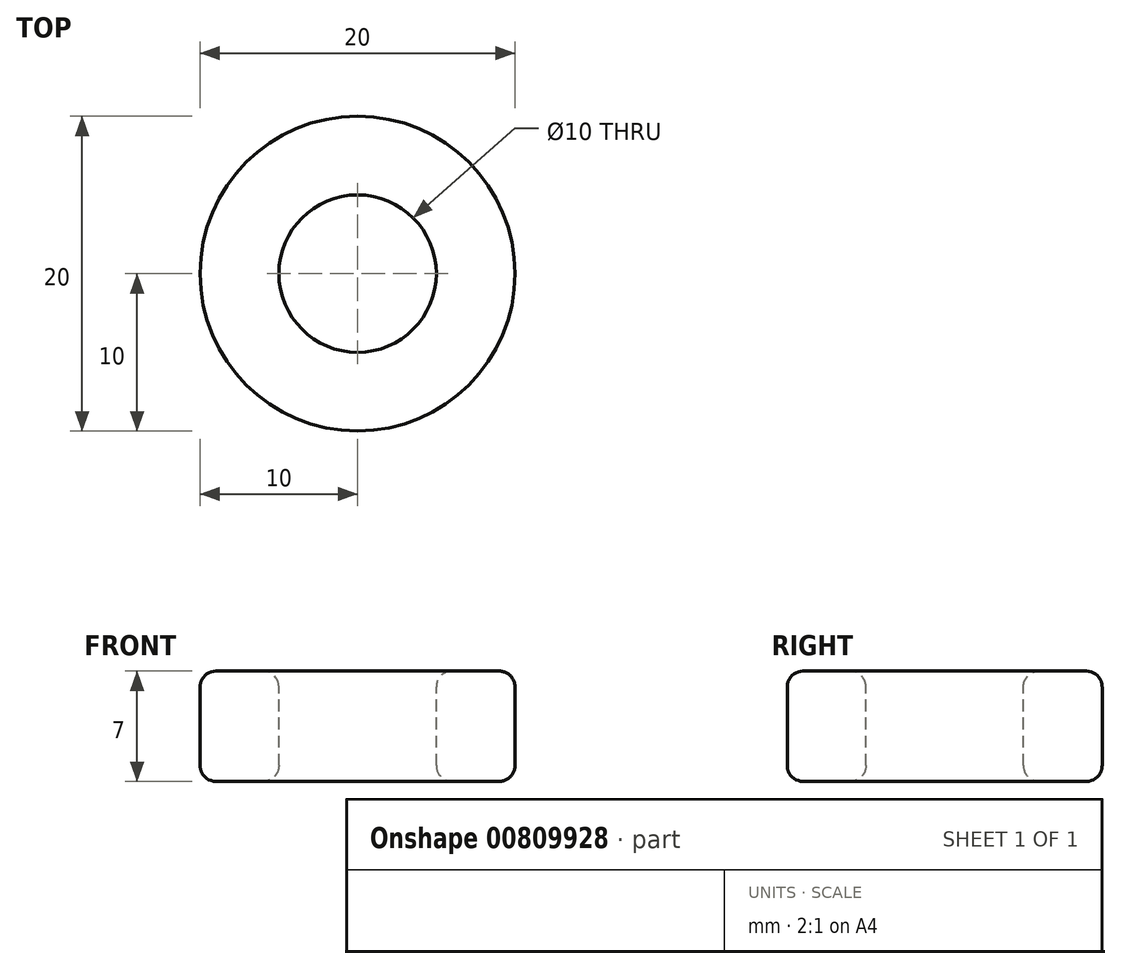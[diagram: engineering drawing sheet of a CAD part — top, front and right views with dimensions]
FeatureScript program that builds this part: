
annotation { "Feature Type Name" : "Feature", "Feature Type Description" : "" }
export const myFeature = defineFeature(function(context is Context, id is Id, definition is map)
    precondition{}
    {
        {
            var Q0;
            Q0=qCreatedBy(makeId("Front.planeOp"),FACE);
            var sketch = newSketch(context, id + "F0", { "sketchPlane" : qUnion([Q0])});
            skLineSegment(sketch, "E0", {"start": v(0, 22.35) * mm, "end": v(0, -14.98) * mm, "construction": true});
            skLineSegment(sketch, "E1.bottom", {"start": v(5, 3.5) * mm, "end": v(10, 3.5) * mm});
            skLineSegment(sketch, "E1.top", {"start": v(5, -3.5) * mm, "end": v(10, -3.5) * mm});
            skLineSegment(sketch, "E1.left", {"start": v(5, 3.5) * mm, "end": v(5, -3.5) * mm});
            skLineSegment(sketch, "E1.right", {"start": v(10, 3.5) * mm, "end": v(10, -3.5) * mm});
            skSolve(sketch);
        }
        {
            var Q0;
            Q0=makeQuery(id+"F0.imprint","IMPRINT",FACE,{"disambiguationData":[TD([[makeQuery(id+"F0.imprint","IMPRINT",EDGE,{"derivedFrom":sQuery(id+"F0.wireOp",EDGE,"E1.bottom")}),-1.0]])]});
            var Q1;
            Q1=sQuery(id+"F0.wireOp",EDGE,"E0");
            revolve(context, id + "F1", {"surfaceOperationType" : NewSurfaceOperationType.NEW, "entities" : qUnion([Q0]), "axis" : qUnion([Q1]), "revolveType" : RevolveType.FULL});
        }
        {
            var Q0;
            Q0=makeQuery(id+"F1.opRevolve","SWEPT_EDGE",EDGE,{"disambiguationData":[OSD([sQuery(id+"F0.wireOp",EDGE,"E1.bottom"),sQuery(id+"F0.wireOp",EDGE,"E1.left")])]});
            var Q1;
            Q1=makeQuery(id+"F1.opRevolve","SWEPT_EDGE",EDGE,{"disambiguationData":[OSD([sQuery(id+"F0.wireOp",EDGE,"E1.bottom"),sQuery(id+"F0.wireOp",EDGE,"E1.right")])]});
            var Q2;
            Q2=makeQuery(id+"F1.opRevolve","SWEPT_EDGE",EDGE,{"disambiguationData":[OSD([sQuery(id+"F0.wireOp",EDGE,"E1.top"),sQuery(id+"F0.wireOp",EDGE,"E1.right")])]});
            var Q3;
            Q3=makeQuery(id+"F1.opRevolve","SWEPT_EDGE",EDGE,{"disambiguationData":[OSD([sQuery(id+"F0.wireOp",EDGE,"E1.top"),sQuery(id+"F0.wireOp",EDGE,"E1.left")])]});
            fillet(context, id + "F2", {"entities" : qUnion([Q0, Q1, Q2, Q3]), "radius" : 1 * mm, "tangentPropagation" : true, "allowEdgeOverflow" : false});
        }
    });
